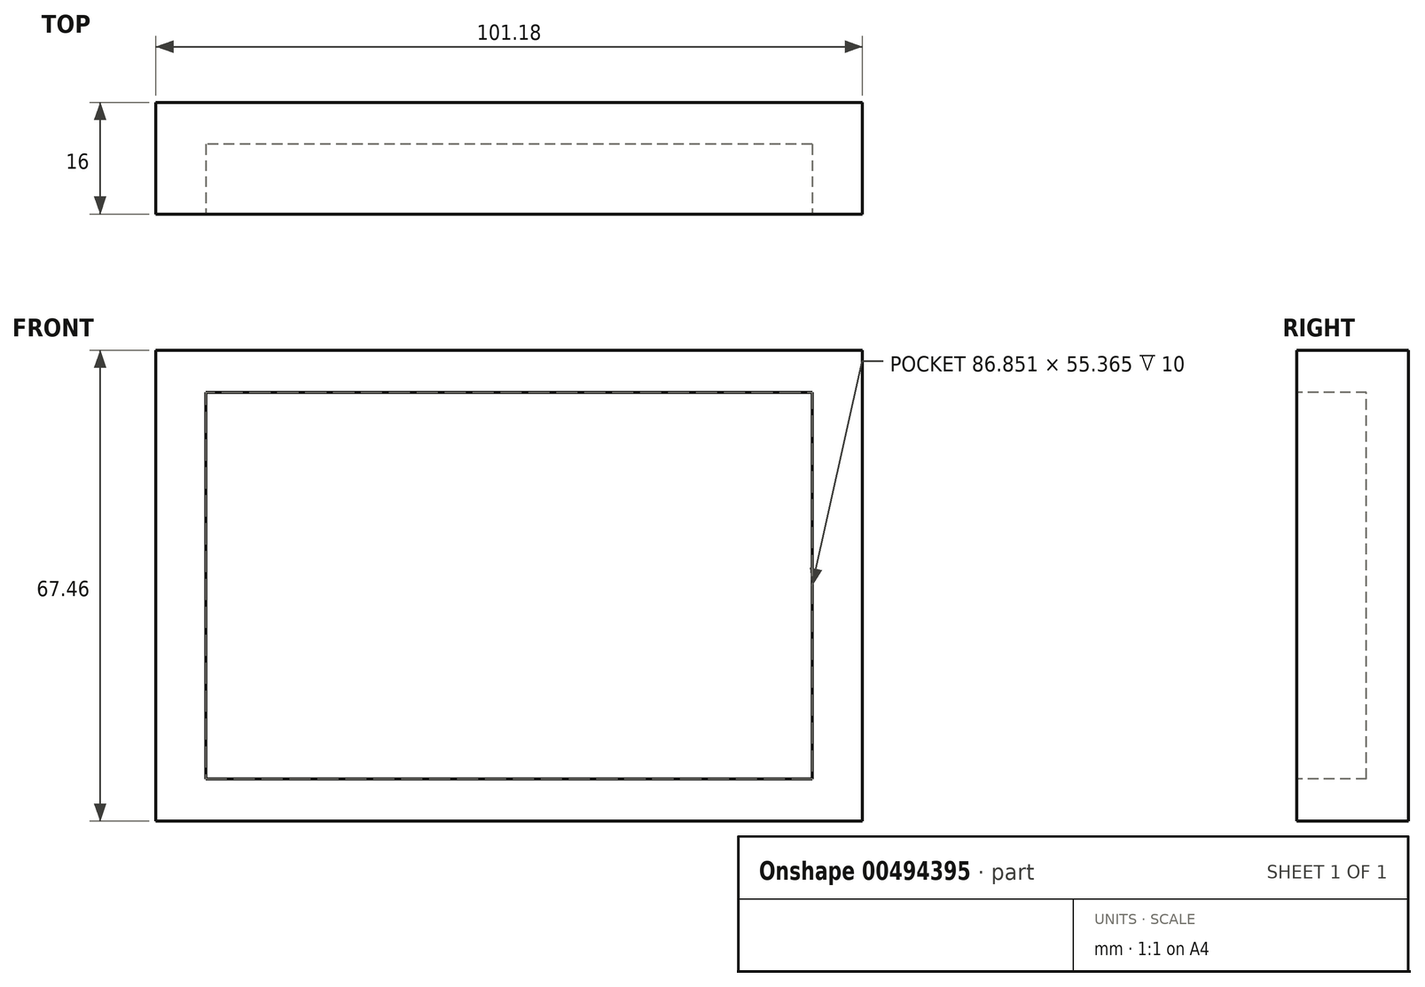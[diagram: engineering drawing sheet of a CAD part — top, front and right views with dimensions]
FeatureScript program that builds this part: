
annotation { "Feature Type Name" : "Feature", "Feature Type Description" : "" }
export const myFeature = defineFeature(function(context is Context, id is Id, definition is map)
    precondition{}
    {
        {
            var Q0;
            Q0=qCreatedBy(makeId("Front.planeOp"),FACE);
            var sketch = newSketch(context, id + "F0", { "sketchPlane" : qUnion([Q0])});
            skLineSegment(sketch, "E0.bottom", {"start": v(0, 0) * mm, "end": v(0, 0) * mm});
            skLineSegment(sketch, "E0.top", {"start": v(0, 0) * mm, "end": v(0, 0) * mm});
            skLineSegment(sketch, "E0.left", {"start": v(0, 0) * mm, "end": v(0, 0) * mm});
            skLineSegment(sketch, "E0.right", {"start": v(0, 0) * mm, "end": v(0, 0) * mm});
            skPoint(sketch, "E0.middle", {"position": v(0, 0) * mm});
            skLineSegment(sketch, "E1.bottom", {"start": v(50.6, -33.73) * mm, "end": v(-50.6, -33.73) * mm});
            skLineSegment(sketch, "E1.top", {"start": v(50.6, 33.73) * mm, "end": v(-50.6, 33.73) * mm});
            skLineSegment(sketch, "E1.left", {"start": v(50.6, -33.73) * mm, "end": v(50.6, 33.73) * mm});
            skLineSegment(sketch, "E1.right", {"start": v(-50.6, -33.73) * mm, "end": v(-50.6, 33.73) * mm});
            skSolve(sketch);
        }
        {
            var Q0;
            Q0=makeQuery(id+"F0.imprint","IMPRINT",FACE,{"disambiguationData":[TD([[makeQuery(id+"F0.imprint","IMPRINT",EDGE,{"derivedFrom":sQuery(id+"F0.wireOp",EDGE,"E1.bottom")}),-1.0]])]});
            extrude(context, id + "F1", {"entities" : qUnion([Q0]), "depth" : 16 * mm});
        }
        {
            var Q0;
            Q0=makeQuery(id+"F1.opExtrude","CAP_FACE",FACE,{"disambiguationData":[OSD([sQuery(id+"F0.wireOp",EDGE,"E1.bottom"),sQuery(id+"F0.wireOp",EDGE,"E1.top"),sQuery(id+"F0.wireOp",EDGE,"E1.left"),sQuery(id+"F0.wireOp",EDGE,"E1.right")])],"isStart":false});
            var sketch = newSketch(context, id + "F2", { "sketchPlane" : qUnion([Q0])});
            skLineSegment(sketch, "E2.bottom", {"start": v(43.43, -27.68) * mm, "end": v(-43.43, -27.68) * mm});
            skLineSegment(sketch, "E2.top", {"start": v(43.43, 27.68) * mm, "end": v(-43.43, 27.68) * mm});
            skLineSegment(sketch, "E2.left", {"start": v(43.43, -27.68) * mm, "end": v(43.43, 27.68) * mm});
            skLineSegment(sketch, "E2.right", {"start": v(-43.43, -27.68) * mm, "end": v(-43.43, 27.68) * mm});
            skPoint(sketch, "E2.middle", {"position": v(0, 0) * mm});
            skSolve(sketch);
        }
        {
            var Q0;
            Q0=makeQuery(id+"F2.imprint","IMPRINT",FACE,{"disambiguationData":[TD([[makeQuery(id+"F2.imprint","IMPRINT",EDGE,{"derivedFrom":sQuery(id+"F2.wireOp",EDGE,"E2.bottom")}),-1.0]])]});
            extrude(context, id + "F3", {"entities" : qUnion([Q0]), "operationType" : NewBodyOperationType.REMOVE, "oppositeDirection" : true, "depth" : 10 * mm});
        }
    });
